# Revit family: Edelstahlrohrschelle V4A, M16, Ø174-277, Gummi
name_source: partatom
category: HLS-Bauteile
revit_build: Autodesk Revit 2017 (Build: 20190507_1515(x64)
units: mm (PartAtom-declared; Revit-internal decimal feet)

## family parameters
Arbeitsebenenbasiert = Ja
Beim Laden mit Abzugskörper schneiden = Nein
Bemaßung runder Anschluss = Durchmesser verwenden
Gemeinsam genutzt = Ja
Immer vertikal = Nein
Raumberechnungspunkt = Nein
Teiletyp = Normal

## types (8) — shared parameters
A = 25 mm  [stored 0.082021 ft]
Anschluss = M16
Anschlußhöhe = 24 mm
Bauart = zweiteilig
Baustoffklasse = B2
DF1 = 29 mm  [stored 0.0951444 ft]
DF2 = 35 mm  [stored 0.114829 ft]
DS = 6 mm  [stored 0.019685 ft]
DVS = 11 mm  [stored 0.0360892 ft]
Dämmstärke = 6 mm  [stored 0.019685 ft]
Fabrikat = MEFA
Farbe Schalldämmeinlage = schwarz
Firma = MEFA Befestigungs- und Montagesysteme GmbH
HGA = 15 mm  [stored 0.0492126 ft]
Kurztext1 = Rohrschelle Edelstahl V4A 35x4,0
MB = 35 mm  [stored 0.114829 ft]
MD = 4 mm  [stored 0.0131234 ft]
Material = Edelstahl
Material Schalldämmeinlage = TPE
Materialmaße = 35x4,0 mm
Mengeneinheit = St
Schalldämmeinlage = Gummi
Verschluss = Schraubenverschluss
Verschluss-Schraube = M10
Vorgabe-Ansicht = 1219 mm
max. Temperaturbeständigkeit = 100 °C
max. zul. Last horizontal = 0.00 kN
max. zul. Last vertikal = 0.00 kN
vpe = 1 St
zero-valued in all types: Nennweite DN Rohr, Rohraußendurchmesser, Stärke Material

## per-type parameters (varying)
| type | AB | Achsabstand | Artikelnummer | B | D | D0 | Dmax | Dmin | EAN | Gewicht | Gewicht pro Bauteil | H | Kurztext2 | R | RM | Rohraußendurchmesser Zoll | S | max. Rohraußendurchmesser | min. Rohraußendurchmesser |
| Edelstahlrohrschelle V4A, M16, Ø174-182, Gummi | 8 mm  [stored 0.0262467 ft] | 236 mm | 0490426 | 266 mm | 182 mm  [stored 0.597113 ft] | 194 mm | 182 mm  [stored 0.597113 ft] | 174 mm  [stored 0.570866 ft] | 4250928413185 | 1.02 kg | 1.02 kg | 217 mm  [stored 0.711942 ft] | 174 - 182 mm M16 TPE | 97 mm | 101 mm | Zoll | 237 mm | 182 mm  [stored 0.597113 ft] | 174 mm  [stored 0.570866 ft] |
| Edelstahlrohrschelle V4A, M16, Ø192-200, Gummi | 8 mm  [stored 0.0262467 ft] | 255 mm | 0490428 | 284 mm | 200 mm  [stored 0.656168 ft] | 212 mm | 200 mm  [stored 0.656168 ft] | 192 mm  [stored 0.629921 ft] | 4250928413192 | 1.09 kg | 1.09 kg | 235 mm | 192 - 200 mm M16 TPE | 106 mm | 110 mm | Zoll | 255 mm | 200 mm  [stored 0.656168 ft] | 192 mm  [stored 0.629921 ft] |
| Edelstahlrohrschelle V4A, M16, Ø201-205, Gummi | 4 mm  [stored 0.0131234 ft] | 261 mm | 0490429 | 289 mm | 205 mm  [stored 0.672572 ft] | 217 mm  [stored 0.711942 ft] | 205 mm  [stored 0.672572 ft] | 201 mm  [stored 0.659449 ft] | 4250928413208 | 1.12 kg | 1.12 kg | 240 mm | 201 - 205 mm M16 TPE | 109 mm | 113 mm  [stored 0.370735 ft] | Zoll | 260 mm | 205 mm  [stored 0.672572 ft] | 201 mm  [stored 0.659449 ft] |
| Edelstahlrohrschelle V4A, M16, Ø206-214, Gummi | 8 mm  [stored 0.0262467 ft] | 269 mm | 0490430 | 298 mm | 214 mm  [stored 0.7021 ft] | 226 mm | 214 mm  [stored 0.7021 ft] | 206 mm  [stored 0.675853 ft] | 4250928413215 | 1.14 kg | 1.14 kg | 249 mm | 206 - 214 mm M16 TPE | 113 mm  [stored 0.370735 ft] | 117 mm | Zoll | 269 mm | 214 mm  [stored 0.7021 ft] | 206 mm  [stored 0.675853 ft] |
| Edelstahlrohrschelle V4A, M16, Ø215-225, Gummi | 9 mm  [stored 0.0295276 ft] | 280 mm | 0490431 | 308 mm | 225 mm | 237 mm | 224 mm | 216 mm  [stored 0.708661 ft] | 4250928413222 | 1.18 kg | 1.18 kg | 260 mm | 215 - 225 mm M16 TPE | 119 mm | 123 mm | 8 Zoll | 279 mm | 225 mm | 215 mm |
| Edelstahlrohrschelle V4A, M16, Ø241-248, Gummi | 7 mm  [stored 0.0229659 ft] | 303 mm | 0492434 | 332 mm | 248 mm | 260 mm | 248 mm | 241 mm | 4250928413253 | 1.29 kg | 1.29 kg | 283 mm | 241 - 248 mm M16 TPE | 130 mm  [stored 0.426509 ft] | 134 mm | Zoll | 303 mm | 248 mm | 241 mm |
| Edelstahlrohrschelle V4A, M16, Ø250-257, Gummi | 7 mm  [stored 0.0229659 ft] | 312 mm | 0492435 | 341 mm | 257 mm | 269 mm | 257 mm | 250 mm | 4250928413260 | 1.32 kg | 1.32 kg | 292 mm | 250 - 257 mm M16 TPE | 135 mm  [stored 0.442913 ft] | 139 mm | Zoll | 312 mm | 257 mm | 250 mm |
| Edelstahlrohrschelle V4A, M16, Ø272-277, Gummi | 5 mm  [stored 0.0164042 ft] | 333 mm | 0492438 | 361 mm | 277 mm | 289 mm | 277 mm | 272 mm | 4250928413277 | 1.41 kg | 1.41 kg | 312 mm | 272 - 277 mm M16 TPE | 145 mm | 149 mm  [stored 0.488845 ft] | 10 Zoll | 332 mm | 277 mm | 272 mm |

note: [stored X ft] marks values corroborated as IEEE doubles in the binary element streams (Revit-internal decimal feet)

## geometry (parser evidence)
native form markers: Sweep x6
no freeform markers — native parametric forms only
